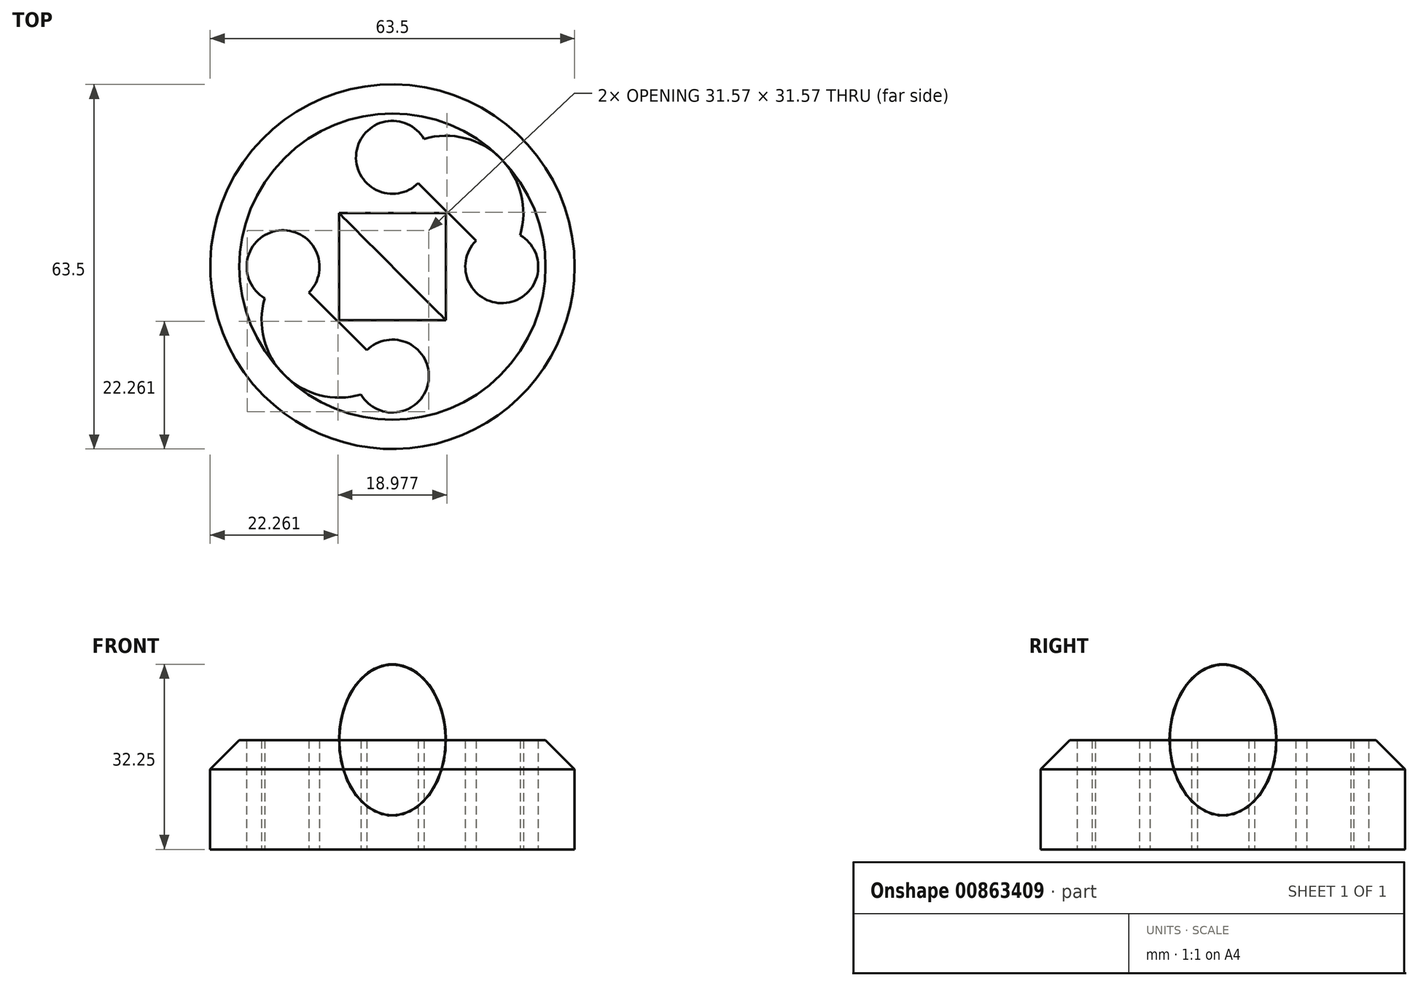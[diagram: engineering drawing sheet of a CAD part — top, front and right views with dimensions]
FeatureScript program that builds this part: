
annotation { "Feature Type Name" : "Feature", "Feature Type Description" : "" }
export const myFeature = defineFeature(function(context is Context, id is Id, definition is map)
    precondition{}
    {
        {
            var Q0;
            Q0=qCreatedBy(makeId("Top.planeOp"),FACE);
            var sketch = newSketch(context, id + "F0", { "sketchPlane" : qUnion([Q0])});
            skCircle(sketch, "E0", {"center": v(0, 0) * mm, "radius": 31.75 * mm});
            skLineSegment(sketch, "E1", {"start": v(-31.75, 0) * mm, "end": v(0, 0) * mm, "construction": true});
            skCircle(sketch, "E2", {"center": v(19.05, 0) * mm, "radius": 6.35 * mm});
            skLineSegment(sketch, "E3", {"start": v(19.05, 0) * mm, "end": v(25.4, 0) * mm, "construction": true});
            skCircle(sketch, "E4", {"center": v(0, 19.05) * mm, "radius": 6.35 * mm});
            skCircle(sketch, "E5", {"center": v(0, -19.05) * mm, "radius": 6.35 * mm});
            skCircle(sketch, "E6", {"center": v(-19.05, 0) * mm, "radius": 6.35 * mm});
            skLineSegment(sketch, "E7", {"start": v(0, 19.05) * mm, "end": v(0, -19.05) * mm});
            skArc(sketch, "E8", {"start": v(19.05, 0) * mm, "mid": v(18.86, 18.86) * mm, "end": v(0, 19.05) * mm});
            skLineSegment(sketch, "E9", {"start": v(0, 19.05) * mm, "end": v(19.05, 0) * mm});
            skLineSegment(sketch, "E10", {"start": v(-19.05, 0) * mm, "end": v(0, -19.05) * mm});
            skArc(sketch, "E11", {"start": v(-19.05, 0) * mm, "mid": v(-18.86, -18.86) * mm, "end": v(0, -19.05) * mm});
            skSolve(sketch);
        }
        {
            var Q0;
            Q0=makeQuery(id+"F0.imprint","IMPRINT",FACE,{"disambiguationData":[TD([[makeQuery(id+"F0.imprint","IMPRINT",EDGE,{"derivedFrom":sQuery(id+"F0.wireOp",EDGE,"E0")}),1.0]])]});
            extrude(context, id + "F1", {"entities" : qUnion([Q0]), "depth" : 19.05 * mm, "offsetDistance" : 25.4 * mm});
        }
        {
            var Q0;
            Q0=makeQuery(id+"F1.opExtrude","CAP_EDGE",EDGE,{"disambiguationData":[OSD([sQuery(id+"F0.wireOp",EDGE,"E0")])],"isStart":false});
            chamfer(context, id + "F2", {"entities" : qUnion([Q0]), "width" : 5.08 * mm, "tangentPropagation" : true});
        }
        {
            var Q0;
            Q0=makeQuery(id+"F1.opExtrude","CAP_FACE",FACE,{"disambiguationData":[OSD([sQuery(id+"F0.wireOp",EDGE,"E0"),sQuery(id+"F0.wireOp",EDGE,"E2"),sQuery(id+"F0.wireOp",EDGE,"E4"),sQuery(id+"F0.wireOp",EDGE,"E5"),sQuery(id+"F0.wireOp",EDGE,"E6"),sQuery(id+"F0.wireOp",EDGE,"E8"),sQuery(id+"F0.wireOp",EDGE,"E9"),sQuery(id+"F0.wireOp",EDGE,"E10"),sQuery(id+"F0.wireOp",EDGE,"E11")])],"isStart":false});
            var sketch = newSketch(context, id + "F3", { "sketchPlane" : qUnion([Q0])});
            skPoint(sketch, "E12.endSnap0", {"position": v(9.52, 9.53) * mm});
            skLineSegment(sketch, "E13", {"start": v(-9.33, -9.33) * mm, "end": v(9.33, -9.33) * mm});
            skLineSegment(sketch, "E14", {"start": v(-9.33, -9.33) * mm, "end": v(0, 0) * mm});
            skLineSegment(sketch, "E15", {"start": v(0, 0) * mm, "end": v(9.33, -9.33) * mm});
            skLineSegment(sketch, "E16.MirrorCS", {"start": v(9.33, 9.33) * mm, "end": v(9.33, -9.33) * mm});
            skLineSegment(sketch, "E17.MirrorCS", {"start": v(9.33, 9.33) * mm, "end": v(0, 0) * mm});
            skLineSegment(sketch, "E18.MirrorCS", {"start": v(9.33, 9.33) * mm, "end": v(-9.33, 9.33) * mm});
            skLineSegment(sketch, "E19.MirrorCS", {"start": v(0, 0) * mm, "end": v(-9.33, 9.33) * mm});
            skLineSegment(sketch, "E20.MirrorCS", {"start": v(-9.33, -9.33) * mm, "end": v(-9.33, 9.33) * mm});
            skSolve(sketch);
        }
        {
            var Q0;
            Q0=makeQuery(id+"F3.imprint","IMPRINT",FACE,{"disambiguationData":[TD([[makeQuery(id+"F3.imprint","IMPRINT",EDGE,{"derivedFrom":sQuery(id+"F3.wireOp",EDGE,"E13")}),1.0]])]});
            var Q1;
            Q1=sQuery(id+"F3.wireOp",EDGE,"E14");
            revolve(context, id + "F4", {"operationType" : NewBodyOperationType.ADD, "surfaceOperationType" : NewSurfaceOperationType.NEW, "entities" : qUnion([Q0]), "axis" : qUnion([Q1]), "revolveType" : RevolveType.FULL});
        }
        {
            var Q0;
            Q0=makeQuery(id+"F3.imprint","IMPRINT",FACE,{"disambiguationData":[TD([[makeQuery(id+"F3.imprint","IMPRINT",EDGE,{"derivedFrom":sQuery(id+"F3.wireOp",EDGE,"E15")}),1.0]])]});
            var Q1;
            Q1=sQuery(id+"F3.wireOp",EDGE,"E17.MirrorCS");
            revolve(context, id + "F5", {"operationType" : NewBodyOperationType.ADD, "surfaceOperationType" : NewSurfaceOperationType.NEW, "entities" : qUnion([Q0]), "axis" : qUnion([Q1]), "revolveType" : RevolveType.FULL});
        }
    });
